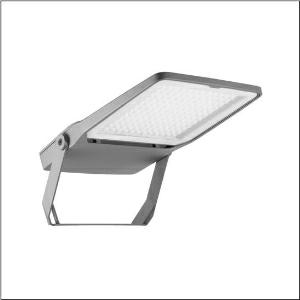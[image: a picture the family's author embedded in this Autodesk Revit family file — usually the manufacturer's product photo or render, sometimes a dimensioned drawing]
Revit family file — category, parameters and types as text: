
# Revit family: floodlight_fl_20_midi___pl52_5xa7681d2d1ac_0834
name_source: partatom
category: Lighting Fixtures
units: mm (PartAtom-declared; Revit-internal decimal feet)

## family parameters
Cut with Voids When Loaded = No
Host = Face
Light Source = No
Part Type = Normal
Room Calculation Point = No
Round Connector Dimension = Use Diameter
Shared = No

## types (1)
- Floodlight FL 20 midi  PL52 (1 x LED 4000K / CRI = 70 (unbekannt), 17990 lm, 4000K)
    Apparent Load = 142 VA
    CIE Flux Codes = 27 59 98 100 100
    Color Rendering = 70
    Color Temperature = 4000K
    Default Elevation = 1800 mm
    Description = Floodlight FL 20 midi, floodlight, primary light control with lens, of plastic, primary optical cover: protective disc, of toughened safety glass, transparent, light distribution: PL52, light emission: direct distribution, primary light characteristic: asymmetric, installation type: surface-mounted, LED, High Power LED, rated luminous flux: 17.990lm, luminous efficacy: 127lm/W, light colour: 740, colour temperature: 4000K, control gear: ECG Basic, control: power reduction, overheat protection, electronic power reduction, with terminal, 5-pole, max. 2.5mm², mains connection: 220..240V, AC, 50/60Hz, rated input power: 142W, LED unit, of diecast aluminium, powder-coated, Siteco® metallic grey (DB 702S), corrosivity category C5 mid according to DIN EN ISO 12944, incl. 1x M20 cable gland for cable Ø 6.5..12mm, length: 654mm, width: 450mm, height: 76mm, housing frame, of diecast aluminium, powder-coated, Siteco® metallic grey (DB 702S), mounting bracket, of steel, powder-coated, Siteco® metallic grey (DB 702S), ON/OFF, protection rating (complete): IP66, insulation class (complete): insulation class I (protective earthing), certification: CE, ENEC, VDE, protection symbol: D, permissible operating ambient temperature: -40..+40°C, permissible operating ambient temperature for outdoor applications: -40..+50°C, standard: DIN EN 12944, packaging unit: 1 piece

Light Distribution: PL52
    Height = 76 mm
    Lamp = 1 x LED 4000K / CRI >= 70 (unbekannt)
    Lamp Light Flux = 17990 lm
    Lamp count = 1
    Length = 672 mm
    Luminous efficacy = 127 lm/W
    Manufacturer = Siteco
    ModVariant = No
    Model = 5XA7681D2D1AC
    Mounting Place = Wall
    Mounting Type = Surface mounted
    Number of Poles = 1
    OnlyDefault = Yes
    Power Factor = 1
    Product Name = Floodlight FL 20 midi | PL52
    Product group = floodlight | wall mounted
    ProductGroupID = 2001
    Protection Class = Protection class I
    Protection Degree = IP 66
    RLX_Detail_Level = 1
    RLX_Emergency_Light_Flux = 0 lm
    RLX_Emergency_Type = 0
    RLX_Emergency_Type_DB = No
    RlxData = <blob elided: 94233 chars, md5=2d2caf2b>
    Socket = socket
    Standby Power = 0 W
    System Light Flux = 17990 lm
    System Power = 142 W
    Type Comments = Product without accessories
    Type Image = l_1005943.jpg
    URL = http://relux.com
    VarID = ---
    Voltage = 0 V
    Weight = 0.00 kg
    Width = 450 mm

## geometry (parser evidence)
native form markers: Blend x4, Sweep x13
no freeform markers — native parametric forms only
